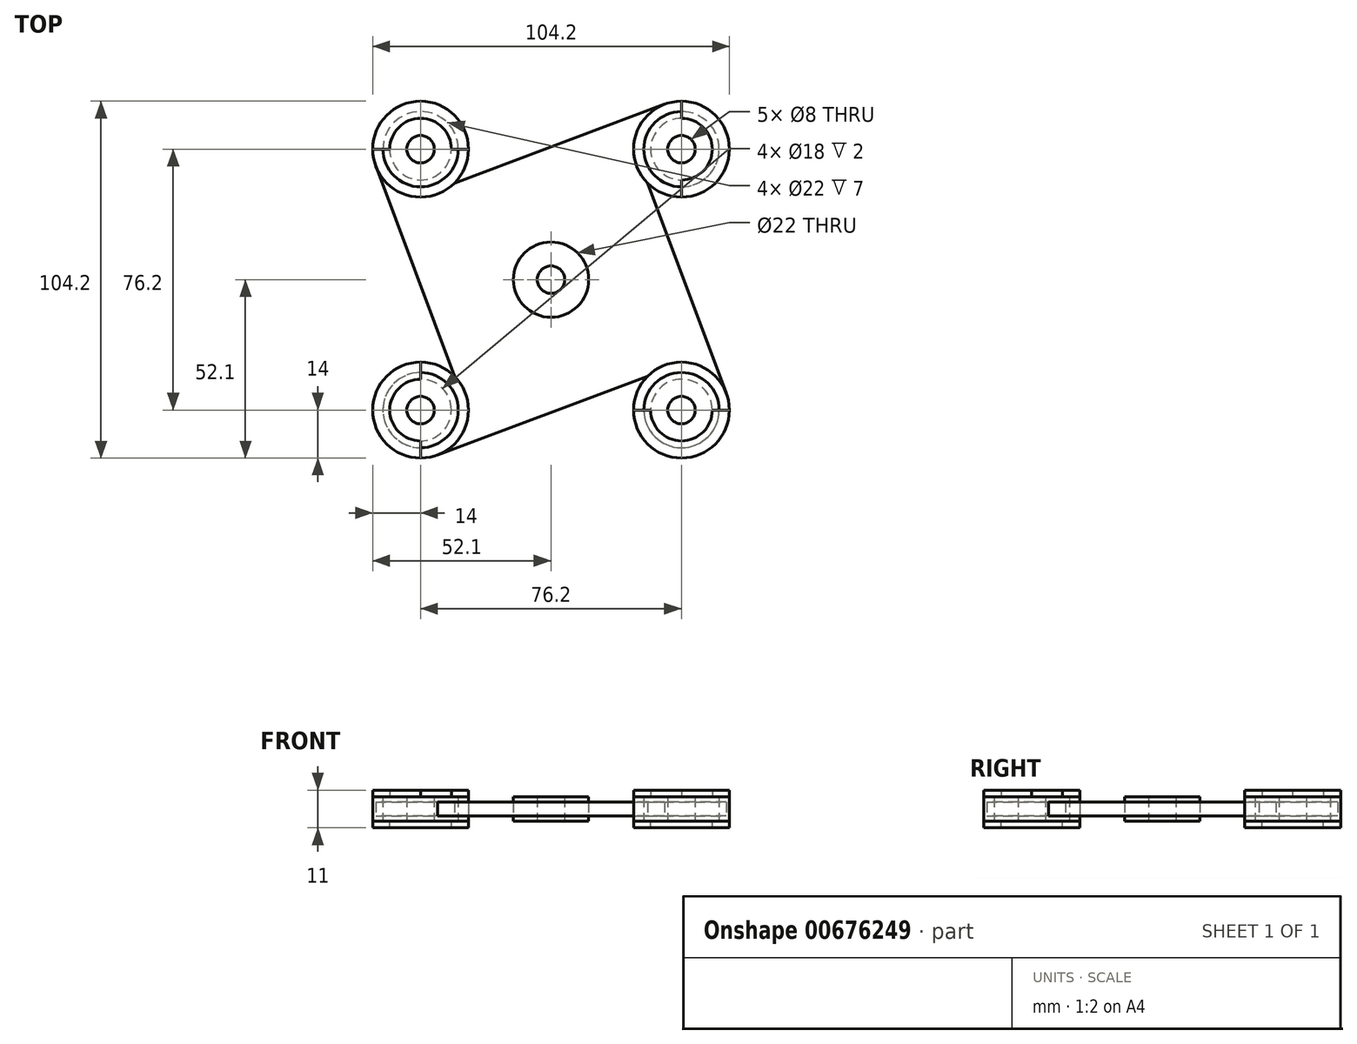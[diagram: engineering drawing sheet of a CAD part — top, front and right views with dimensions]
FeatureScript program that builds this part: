
annotation { "Feature Type Name" : "Feature", "Feature Type Description" : "" }
export const myFeature = defineFeature(function(context is Context, id is Id, definition is map)
    precondition{}
    {
        {
            var Q0;
            Q0=qCreatedBy(makeId("Top.planeOp"),FACE);
            var sketch = newSketch(context, id + "F0", { "sketchPlane" : qUnion([Q0])});
            skLineSegment(sketch, "E0.bottom", {"start": v(0, 0) * mm, "end": v(76.2, 0) * mm, "construction": true});
            skLineSegment(sketch, "E0.top", {"start": v(0, -76.2) * mm, "end": v(76.2, -76.2) * mm, "construction": true});
            skLineSegment(sketch, "E0.left", {"start": v(0, 0) * mm, "end": v(0, -76.2) * mm, "construction": true});
            skLineSegment(sketch, "E0.right", {"start": v(76.2, 0) * mm, "end": v(76.2, -76.2) * mm, "construction": true});
            skCircle(sketch, "E1", {"center": v(0, 0) * mm, "radius": 11 * mm});
            skCircle(sketch, "E2", {"center": v(76.2, 0) * mm, "radius": 11 * mm});
            skCircle(sketch, "E3", {"center": v(76.2, -76.2) * mm, "radius": 11 * mm});
            skCircle(sketch, "E4", {"center": v(0, -76.2) * mm, "radius": 11 * mm});
            skCircle(sketch, "E5", {"center": v(0, -76.2) * mm, "radius": 4 * mm});
            skCircle(sketch, "E6", {"center": v(0, 0) * mm, "radius": 4 * mm});
            skCircle(sketch, "E7", {"center": v(76.2, 0) * mm, "radius": 4 * mm});
            skCircle(sketch, "E8", {"center": v(76.2, -76.2) * mm, "radius": 4 * mm});
            skLineSegment(sketch, "E9", {"start": v(0, -76.2) * mm, "end": v(76.2, 0) * mm, "construction": true});
            skLineSegment(sketch, "E10", {"start": v(76.2, -76.2) * mm, "end": v(0, 0) * mm, "construction": true});
            skCircle(sketch, "E11", {"center": v(38.1, -38.1) * mm, "radius": 4 * mm});
            skCircle(sketch, "E12", {"center": v(38.1, -38.1) * mm, "radius": 11 * mm});
            skCircle(sketch, "E13", {"center": v(0, 0) * mm, "radius": 14 * mm});
            skCircle(sketch, "E14", {"center": v(76.2, 0) * mm, "radius": 14 * mm});
            skCircle(sketch, "E15", {"center": v(76.2, -76.2) * mm, "radius": 14 * mm});
            skCircle(sketch, "E16", {"center": v(0, -76.2) * mm, "radius": 14 * mm});
            skLineSegment(sketch, "E17", {"start": v(9.9, -9.9) * mm, "end": v(71.29, 13.1) * mm});
            skLineSegment(sketch, "E18", {"start": v(71.29, 13.1) * mm, "end": v(76.2, 0) * mm});
            skLineSegment(sketch, "E19", {"start": v(66.3, -9.9) * mm, "end": v(89.3, -71.29) * mm});
            skLineSegment(sketch, "E20", {"start": v(89.3, -71.29) * mm, "end": v(76.2, -76.2) * mm});
            skLineSegment(sketch, "E21", {"start": v(66.3, -66.3) * mm, "end": v(4.91, -89.3) * mm});
            skLineSegment(sketch, "E22", {"start": v(4.91, -89.3) * mm, "end": v(0, -76.2) * mm});
            skLineSegment(sketch, "E23", {"start": v(9.9, -66.3) * mm, "end": v(-13.1, -4.91) * mm});
            skLineSegment(sketch, "E24", {"start": v(-13.1, -4.91) * mm, "end": v(0, 0) * mm});
            skSolve(sketch);
        }
        {
            var Q0;
            Q0=makeQuery(id+"F0.imprint","IMPRINT",FACE,{"disambiguationData":[TD([[makeQuery(id+"F0.imprint","IMPRINT",EDGE,{"derivedFrom":sQuery(id+"F0.wireOp",EDGE,"E6")}),-1.0]])]});
            var Q1;
            Q1=makeQuery(id+"F0.imprint","IMPRINT",FACE,{"disambiguationData":[TD([[makeQuery(id+"F0.imprint","IMPRINT",EDGE,{"derivedFrom":sQuery(id+"F0.wireOp",EDGE,"E7")}),-1.0]])]});
            var Q2;
            Q2=makeQuery(id+"F0.imprint","IMPRINT",FACE,{"disambiguationData":[TD([[makeQuery(id+"F0.imprint","IMPRINT",EDGE,{"derivedFrom":sQuery(id+"F0.wireOp",EDGE,"E11")}),-1.0]])]});
            var Q3;
            Q3=makeQuery(id+"F0.imprint","IMPRINT",FACE,{"disambiguationData":[TD([[makeQuery(id+"F0.imprint","IMPRINT",EDGE,{"derivedFrom":sQuery(id+"F0.wireOp",EDGE,"E8")}),-1.0]])]});
            var Q4;
            Q4=makeQuery(id+"F0.imprint","IMPRINT",FACE,{"disambiguationData":[TD([[makeQuery(id+"F0.imprint","IMPRINT",EDGE,{"derivedFrom":sQuery(id+"F0.wireOp",EDGE,"E5")}),-1.0]])]});
            extrude(context, id + "F1", {"entities" : qUnion([Q0, Q1, Q2, Q3, Q4]), "endBound" : BoundingType.SYMMETRIC, "depth" : 7 * mm, "offsetDistance" : 25 * mm});
        }
        {
            var Q0;
            Q0=makeQuery(id+"F0.imprint","IMPRINT",FACE,{"disambiguationData":[TD([[makeQuery(id+"F0.imprint","IMPRINT",EDGE,{"derivedFrom":sQuery(id+"F0.wireOp",EDGE,"E12")}),-1.0]])]});
            extrude(context, id + "F2", {"entities" : qUnion([Q0]), "endBound" : BoundingType.SYMMETRIC, "depth" : 4 * mm, "offsetDistance" : 25 * mm});
        }
        {
            var Q0;
            Q0=makeQuery(id+"F0.imprint","IMPRINT",FACE,{"disambiguationData":[TD([[makeQuery(id+"F0.imprint","IMPRINT",EDGE,{"derivedFrom":sQuery(id+"F0.wireOp",EDGE,"E4")}),-1.0]])]});
            var Q1;
            Q1=makeQuery(id+"F0.imprint","IMPRINT",FACE,{"disambiguationData":[TD([[makeQuery(id+"F0.imprint","IMPRINT",EDGE,{"derivedFrom":sQuery(id+"F0.wireOp",EDGE,"E3")}),-1.0]])]});
            var Q2;
            Q2=makeQuery(id+"F0.imprint","IMPRINT",FACE,{"disambiguationData":[TD([[makeQuery(id+"F0.imprint","IMPRINT",EDGE,{"derivedFrom":sQuery(id+"F0.wireOp",EDGE,"E2")}),-1.0]])]});
            var Q3;
            Q3=makeQuery(id+"F0.imprint","IMPRINT",FACE,{"disambiguationData":[TD([[makeQuery(id+"F0.imprint","IMPRINT",EDGE,{"derivedFrom":sQuery(id+"F0.wireOp",EDGE,"E1")}),-1.0]])]});
            extrude(context, id + "F3", {"entities" : qUnion([Q0, Q1, Q2, Q3]), "endBound" : BoundingType.SYMMETRIC, "depth" : 7 * mm, "offsetDistance" : 25 * mm});
        }
        {
            var Q0;
            Q0=makeQuery(id+"F3.opExtrude","CAP_FACE",FACE,{"disambiguationData":[OSD([sQuery(id+"F0.wireOp",EDGE,"E3"),sQuery(id+"F0.wireOp",EDGE,"E15")])],"isStart":false});
            var sketch = newSketch(context, id + "F4", { "sketchPlane" : qUnion([Q0])});
            skCircle(sketch, "E25.0", {"center": v(76.2, -76.2) * mm, "radius": 14 * mm});
            skCircle(sketch, "E25.1", {"center": v(76.2, 0) * mm, "radius": 14 * mm});
            skCircle(sketch, "E25.2", {"center": v(0, 0) * mm, "radius": 14 * mm});
            skCircle(sketch, "E25.3", {"center": v(0, -76.2) * mm, "radius": 14 * mm});
            skCircle(sketch, "E26.0", {"center": v(0, 0) * mm, "radius": 11 * mm});
            skCircle(sketch, "E26.1", {"center": v(76.2, 0) * mm, "radius": 11 * mm});
            skCircle(sketch, "E26.2", {"center": v(76.2, -76.2) * mm, "radius": 11 * mm});
            skCircle(sketch, "E26.3", {"center": v(0, -76.2) * mm, "radius": 11 * mm});
            skLineSegment(sketch, "E27", {"start": v(-14, 0) * mm, "end": v(-11, 0) * mm});
            skLineSegment(sketch, "E28", {"start": v(11, 0) * mm, "end": v(14, 0) * mm});
            skLineSegment(sketch, "E29", {"start": v(87.2, -76.2) * mm, "end": v(90.2, -76.2) * mm});
            skLineSegment(sketch, "E30", {"start": v(65.2, -76.2) * mm, "end": v(62.2, -76.2) * mm});
            skCircle(sketch, "E31", {"center": v(0, 0) * mm, "radius": 9 * mm});
            skCircle(sketch, "E32", {"center": v(76.2, 0) * mm, "radius": 9 * mm});
            skCircle(sketch, "E33", {"center": v(76.2, -76.2) * mm, "radius": 9 * mm});
            skCircle(sketch, "E34", {"center": v(0, -76.2) * mm, "radius": 9 * mm});
            skLineSegment(sketch, "E35", {"start": v(-11, 0) * mm, "end": v(-9, 0) * mm});
            skLineSegment(sketch, "E36", {"start": v(11, 0) * mm, "end": v(9, 0) * mm});
            skLineSegment(sketch, "E37", {"start": v(87.2, -76.2) * mm, "end": v(85.2, -76.2) * mm});
            skLineSegment(sketch, "E38", {"start": v(67.2, -76.2) * mm, "end": v(65.2, -76.2) * mm});
            skLineSegment(sketch, "E39", {"start": v(76.2, -9) * mm, "end": v(76.2, -14) * mm});
            skLineSegment(sketch, "E40", {"start": v(76.2, 9) * mm, "end": v(76.2, 14) * mm});
            skLineSegment(sketch, "E41", {"start": v(0, -62.2) * mm, "end": v(0, -67.2) * mm});
            skLineSegment(sketch, "E42", {"start": v(0, -85.2) * mm, "end": v(0, -90.2) * mm});
            skSolve(sketch);
        }
        {
            var Q0;
            {var subQ0=sQuery(id+"F4.wireOp",EDGE,"E27");Q0=makeQuery(id+"F4.imprint","IMPRINT",FACE,{"disambiguationData":[TD([[makeQuery(id+"F4.imprint","IMPRINT",EDGE,{"derivedFrom":subQ0}),1.0]])]});}
            var Q1;
            {var subQ0=sQuery(id+"F4.wireOp",EDGE,"E35");Q1=makeQuery(id+"F4.imprint","IMPRINT",FACE,{"disambiguationData":[TD([[makeQuery(id+"F4.imprint","IMPRINT",EDGE,{"derivedFrom":subQ0}),1.0]])]});}
            var Q2;
            {var subQ0=sQuery(id+"F4.wireOp",EDGE,"E39");var subQ1=sQuery(id+"F4.wireOp",EDGE,"E26.1");var subQ2=makeQuery(id+"F4.imprint","INTERSECT",VERTEX,{"derivedFrom":[subQ1,subQ0]});Q2=makeQuery(id+"F4.imprint","IMPRINT",FACE,{"disambiguationData":[TD([[makeQuery(id+"F4.imprint","IMPRINT",EDGE,{"disambiguationData":[TD([[subQ2,-1.0]])],"derivedFrom":subQ1}),1.0]])]});}
            var Q3;
            {var subQ0=sQuery(id+"F4.wireOp",EDGE,"E39");var subQ1=sQuery(id+"F4.wireOp",EDGE,"E25.1");var subQ2=makeQuery(id+"F4.imprint","INTERSECT",VERTEX,{"derivedFrom":[subQ1,subQ0]});Q3=makeQuery(id+"F4.imprint","IMPRINT",FACE,{"disambiguationData":[TD([[makeQuery(id+"F4.imprint","IMPRINT",EDGE,{"disambiguationData":[TD([[subQ2,-1.0]])],"derivedFrom":subQ1}),1.0]])]});}
            var Q4;
            {var subQ0=sQuery(id+"F4.wireOp",EDGE,"E37");Q4=makeQuery(id+"F4.imprint","IMPRINT",FACE,{"disambiguationData":[TD([[makeQuery(id+"F4.imprint","IMPRINT",EDGE,{"derivedFrom":subQ0}),1.0]])]});}
            var Q5;
            {var subQ0=sQuery(id+"F4.wireOp",EDGE,"E29");Q5=makeQuery(id+"F4.imprint","IMPRINT",FACE,{"disambiguationData":[TD([[makeQuery(id+"F4.imprint","IMPRINT",EDGE,{"derivedFrom":subQ0}),-1.0]])]});}
            var Q6;
            {var subQ0=sQuery(id+"F4.wireOp",EDGE,"E41");var subQ1=sQuery(id+"F4.wireOp",EDGE,"E26.3");var subQ2=makeQuery(id+"F4.imprint","INTERSECT",VERTEX,{"derivedFrom":[subQ1,subQ0]});Q6=makeQuery(id+"F4.imprint","IMPRINT",FACE,{"disambiguationData":[TD([[makeQuery(id+"F4.imprint","IMPRINT",EDGE,{"disambiguationData":[TD([[subQ2,-1.0]])],"derivedFrom":subQ1}),1.0]])]});}
            var Q7;
            {var subQ0=sQuery(id+"F4.wireOp",EDGE,"E41");var subQ1=sQuery(id+"F4.wireOp",EDGE,"E25.3");var subQ2=makeQuery(id+"F4.imprint","INTERSECT",VERTEX,{"derivedFrom":[subQ1,subQ0]});Q7=makeQuery(id+"F4.imprint","IMPRINT",FACE,{"disambiguationData":[TD([[makeQuery(id+"F4.imprint","IMPRINT",EDGE,{"disambiguationData":[TD([[subQ2,-1.0]])],"derivedFrom":subQ1}),1.0]])]});}
            extrude(context, id + "F5", {"entities" : qUnion([Q0, Q1, Q2, Q3, Q4, Q5, Q6, Q7]), "depth" : 2 * mm, "offsetDistance" : 25 * mm});
        }
        {
            var Q0;
            Q0=makeQuery(id+"F3.opExtrude","CAP_FACE",FACE,{"disambiguationData":[OSD([sQuery(id+"F0.wireOp",EDGE,"E4"),sQuery(id+"F0.wireOp",EDGE,"E16")])],"isStart":true});
            var sketch = newSketch(context, id + "F6", { "sketchPlane" : qUnion([Q0])});
            skCircle(sketch, "E43.0", {"center": v(0, 76.2) * mm, "radius": 14 * mm});
            skCircle(sketch, "E43.1", {"center": v(76.2, 76.2) * mm, "radius": 14 * mm});
            skCircle(sketch, "E43.2", {"center": v(76.2, 0) * mm, "radius": 14 * mm});
            skCircle(sketch, "E43.3", {"center": v(0, 0) * mm, "radius": 14 * mm});
            skCircle(sketch, "E44", {"center": v(0, 76.2) * mm, "radius": 9 * mm});
            skCircle(sketch, "E45", {"center": v(76.2, 76.2) * mm, "radius": 9 * mm});
            skCircle(sketch, "E46", {"center": v(76.2, 0) * mm, "radius": 9 * mm});
            skCircle(sketch, "E47", {"center": v(0, 0) * mm, "radius": 9 * mm});
            skSolve(sketch);
        }
        {
            var Q0;
            Q0=makeQuery(id+"F6.imprint","IMPRINT",FACE,{"disambiguationData":[TD([[makeQuery(id+"F6.imprint","IMPRINT",EDGE,{"derivedFrom":sQuery(id+"F6.wireOp",EDGE,"E44")}),-1.0]])]});
            var Q1;
            Q1=makeQuery(id+"F6.imprint","IMPRINT",FACE,{"disambiguationData":[TD([[makeQuery(id+"F6.imprint","IMPRINT",EDGE,{"derivedFrom":sQuery(id+"F6.wireOp",EDGE,"E43.0")}),-1.0]])]});
            var Q2;
            Q2=makeQuery(id+"F6.imprint","IMPRINT",FACE,{"disambiguationData":[TD([[makeQuery(id+"F6.imprint","IMPRINT",EDGE,{"derivedFrom":sQuery(id+"F6.wireOp",EDGE,"E43.1")}),1.0]])]});
            var Q3;
            Q3=makeQuery(id+"F6.imprint","IMPRINT",FACE,{"disambiguationData":[TD([[makeQuery(id+"F6.imprint","IMPRINT",EDGE,{"derivedFrom":sQuery(id+"F6.wireOp",EDGE,"E43.2")}),1.0]])]});
            var Q4;
            Q4=makeQuery(id+"F6.imprint","IMPRINT",FACE,{"disambiguationData":[TD([[makeQuery(id+"F6.imprint","IMPRINT",EDGE,{"derivedFrom":sQuery(id+"F6.wireOp",EDGE,"E43.3")}),1.0]])]});
            extrude(context, id + "F7", {"entities" : qUnion([Q0, Q1, Q2, Q3, Q4]), "depth" : 2 * mm, "offsetDistance" : 25 * mm});
        }
    });
